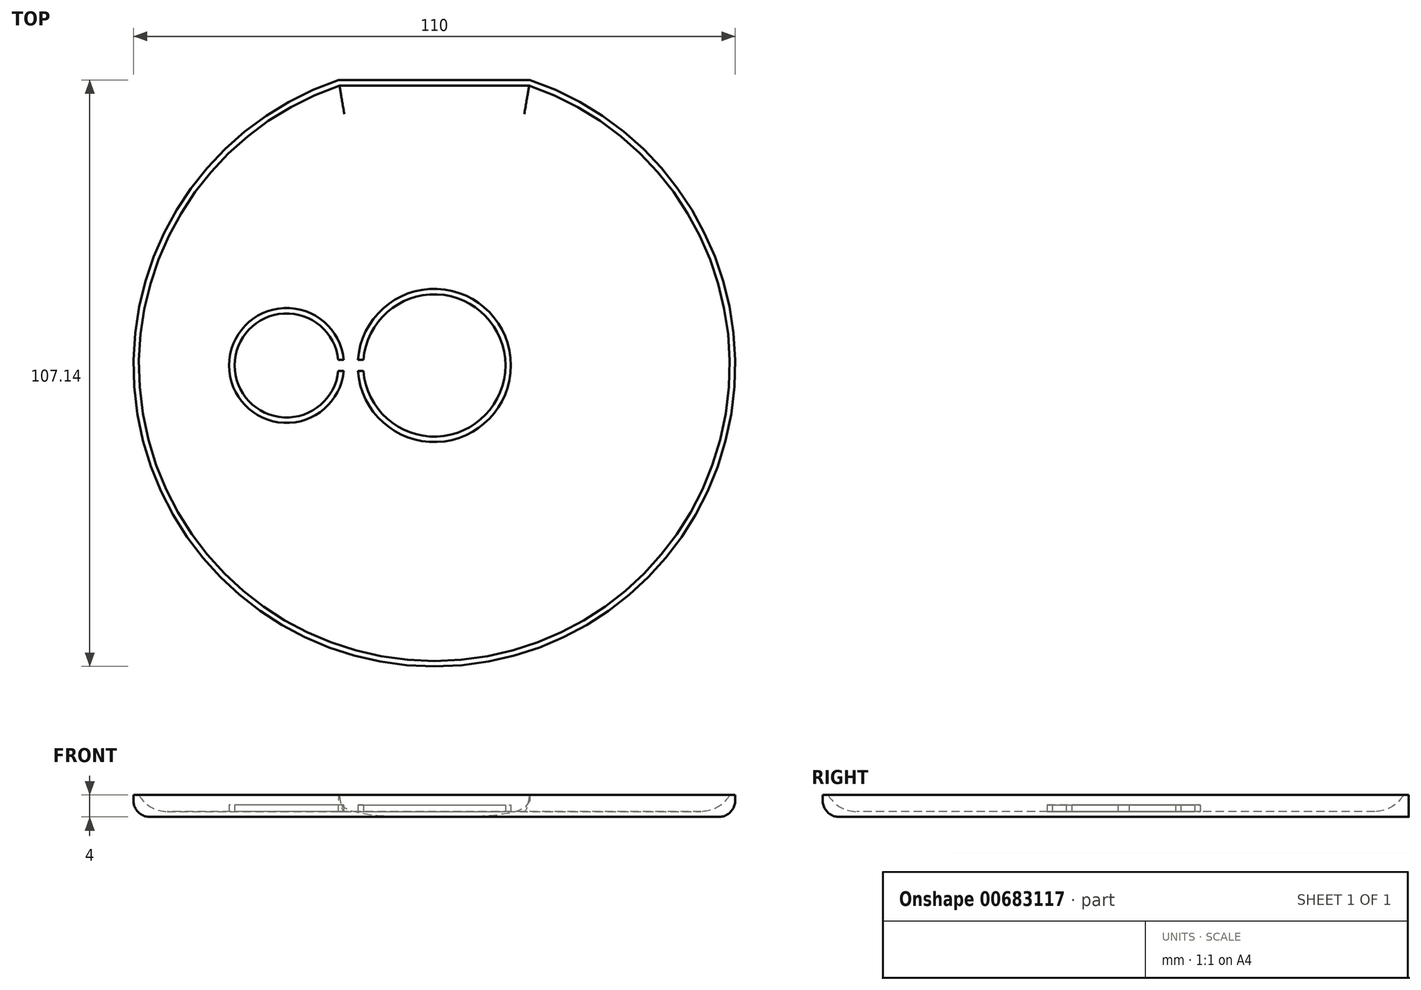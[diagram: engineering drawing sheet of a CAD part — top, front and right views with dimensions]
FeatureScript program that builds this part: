
annotation { "Feature Type Name" : "Feature", "Feature Type Description" : "" }
export const myFeature = defineFeature(function(context is Context, id is Id, definition is map)
    precondition{}
    {
        {
            var Q0;
            Q0=qCreatedBy(makeId("Top.planeOp"),FACE);
            var sketch = newSketch(context, id + "F0", { "sketchPlane" : qUnion([Q0])});
            skArc(sketch, "E0", {"start": v(-17.5, 52.14) * mm, "mid": v(0, -55) * mm, "end": v(17.5, 52.14) * mm});
            skLineSegment(sketch, "E1", {"start": v(-17.5, 52.14) * mm, "end": v(17.5, 52.14) * mm});
            skSolve(sketch);
        }
        {
            var Q0;
            Q0=qSketchRegion(id+"F0",true);
            extrude(context, id + "F1", {"entities" : qUnion([Q0]), "depth" : 4 * mm, "offsetDistance" : 25.4 * mm});
        }
        {
            var Q0;
            Q0=makeQuery(id+"F1.opExtrude","CAP_FACE",FACE,{"disambiguationData":[OSD([sQuery(id+"F0.wireOp",EDGE,"3EveOp2L-82Nq-lBtr-bmo9-LZEQdsZC4kzb.bottom"),sQuery(id+"F0.wireOp",EDGE,"3EveOp2L-82Nq-lBtr-bmo9-LZEQdsZC4kzb.top"),sQuery(id+"F0.wireOp",EDGE,"3EveOp2L-82Nq-lBtr-bmo9-LZEQdsZC4kzb.left"),sQuery(id+"F0.wireOp",EDGE,"3EveOp2L-82Nq-lBtr-bmo9-LZEQdsZC4kzb.right")])],"isStart":false});
            var Q1;
            Q1=makeQuery(id+"F1.opExtrude","CAP_FACE",FACE,{"disambiguationData":[OSD([sQuery(id+"F0.wireOp",EDGE,"E0"),sQuery(id+"F0.wireOp",EDGE,"E1")])],"isStart":false});
            shell(context, id + "F2", {"entities" : qUnion([Q0, Q1]), "thickness" : 1 * mm});
        }
        {
            var Q0;
            Q0=makeQuery(id+"F2.opShell","OFFSET_FACE",FACE,{"disambiguationData":[OSD([sQuery(id+"F0.wireOp",EDGE,"E0"),sQuery(id+"F0.wireOp",EDGE,"E1")])]});
            fillet(context, id + "F3", {"entities" : qUnion([Q0]), "radius" : 6 * mm, "tangentPropagation" : true, "allowEdgeOverflow" : false});
        }
        {
            var Q0;
            Q0=makeQuery(id+"F1.opExtrude","CAP_EDGE",EDGE,{"disambiguationData":[OSD([sQuery(id+"F0.wireOp",EDGE,"E0")])],"isStart":true});
            fillet(context, id + "F4", {"entities" : qUnion([Q0]), "radius" : 3 * mm, "tangentPropagation" : true, "allowEdgeOverflow" : false});
        }
        {
            var Q0;
            Q0=makeQuery(id+"F2.opShell","OFFSET_FACE",FACE,{"disambiguationData":[OSD([sQuery(id+"F0.wireOp",EDGE,"E0"),sQuery(id+"F0.wireOp",EDGE,"E1")])]});
            var sketch = newSketch(context, id + "F5", { "sketchPlane" : qUnion([Q0])});
            skCircle(sketch, "E2", {"center": v(-27, 0) * mm, "radius": 9.5 * mm});
            skCircle(sketch, "E3", {"center": v(-27, 0) * mm, "radius": 10.5 * mm});
            skCircle(sketch, "E4", {"center": v(0, 0) * mm, "radius": 14 * mm});
            skCircle(sketch, "E5", {"center": v(0, 0) * mm, "radius": 13 * mm});
            skSolve(sketch);
        }
        {
            var Q0;
            Q0 = qSketchRegion(id + "F5", true);
            extrude(context, id + "F6", {"entities" : qUnion([Q0]), "operationType" : NewBodyOperationType.ADD, "depth" : 1.2 * mm, "offsetDistance" : 25 * mm});
        }
        {
            var Q0;
            Q0=makeQuery(id+"F5.imprint","IMPRINT",FACE,{"disambiguationData":[TD([[makeQuery(id+"F5.imprint","IMPRINT",EDGE,{"derivedFrom":sQuery(id+"F5.wireOp",EDGE,"E3")}),-1.0]])]});
            var sketch = newSketch(context, id + "F7", { "sketchPlane" : qUnion([Q0])});
            skLineSegment(sketch, "E6.bottom", {"start": v(-18.5, 1) * mm, "end": v(-12, 1) * mm});
            skLineSegment(sketch, "E6.top", {"start": v(-18.5, -1) * mm, "end": v(-12, -1) * mm});
            skLineSegment(sketch, "E6.left", {"start": v(-18.5, 1) * mm, "end": v(-18.5, -1) * mm});
            skLineSegment(sketch, "E6.right", {"start": v(-12, 1) * mm, "end": v(-12, -1) * mm});
            skPoint(sketch, "E7", {"position": v(-12, 0) * mm});
            skSolve(sketch);
        }
        {
            var Q0;
            Q0=qSketchRegion(id+"F7",true);
            extrude(context, id + "F8", {"entities" : qUnion([Q0]), "operationType" : NewBodyOperationType.REMOVE, "depth" : 25 * mm, "offsetDistance" : 25 * mm});
        }
    });
